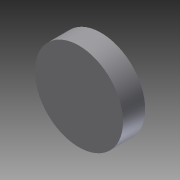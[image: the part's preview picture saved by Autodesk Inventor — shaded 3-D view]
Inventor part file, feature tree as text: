
AUTODESK INVENTOR PART (.ipt)
format: ipt  version: 2012 (Build 160160000, 160)  size: 69,632 bytes
history: native  units: in
note: dims shown in document units (in); Inventor stores cm internally (conversion verified against a paired STEP export)
features: extrude x1, sketch x1
ambient origin geometry x8: Origin, YZ Plane, XZ Plane, XY Plane, X Axis, Y Axis, Z Axis, Center Point
bodies: Solid1 (feature_tree)
feature tree (2):
  extrude  "Extrusion1"  Depth=0.1575in TaperAngle=0.0deg
  sketch  "Sketch1"  dims[d0=0.6264in d1=0.1575in d2=0.0in]
